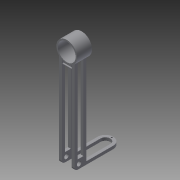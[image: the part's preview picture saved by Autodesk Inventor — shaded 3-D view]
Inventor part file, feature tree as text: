
AUTODESK INVENTOR PART (.ipt)
format: ipt  version: 2015 (Build 190159000, 159)  size: 225,792 bytes
history: native  units: mm
features: extrude x18, sketch x18, plane x2, fillet x1
ambient origin geometry x8: Origin, YZ Plane, XZ Plane, XY Plane, X Axis, Y Axis, Z Axis, Center Point
bodies: Solid1 (feature_tree)
feature tree (39):
  extrude  "Extrusion1"  Depth=2.25mm
  extrude  "Extrusion2"  Depth=2.0mm
  extrude  "Extrusion3"  Depth=10.5mm
  extrude  "Extrusion4"  Depth=2.0mm
  extrude  "Extrusion5"  Depth=2.0mm
  extrude  "Extrusion6"  Depth=2.0mm TaperAngle=0.0deg
  extrude  "Extrusion7"  Depth=6.0mm
  plane  "Work Plane1"
  extrude  "Extrusion8"  Depth=6.0mm
  plane  "Work Plane2"
  extrude  "Extrusion9"  Depth=6.0mm TaperAngle=0.0deg
  extrude  "Extrusion10"  Depth=2.0mm
  extrude  "Extrusion11"  Depth=6.0mm
  extrude  "Extrusion12"  Depth=4.0mm TaperAngle=0.0deg
  extrude  "Extrusion13"  TaperAngle=0.0deg  [1 undecoded]
  extrude  "Extrusion14"  Depth=2.0mm
  extrude  "Extrusion15"  Depth=1.5mm TaperAngle=0.0deg
  extrude  "Extrusion16"  Depth=1.5mm TaperAngle=0.0deg
  fillet  "Fillet4"  Radius=1.0mm
  extrude  "Extrusion17"  Depth=2.0mm
  extrude  "Extrusion18"  Depth=2.0mm
  sketch  "Sketch1"  dims[d0=15.0mm d1=2.25mm]
  sketch  "Sketch2"  dims[d2=2.0mm d3=4.5mm]
  sketch  "Sketch3"  dims[d4=2.0mm d5=10.5mm]
  sketch  "Sketch4"  dims[d6=10.75mm d7=2.0mm]
  sketch  "Sketch5"  dims[d8=13.0mm d9=2.0mm]
  sketch  "Sketch6"  dims[d10=2.0mm d11=60.0mm d12=0.0mm]
  sketch  "Sketch7"  dims[d13=2.0mm d14=6.0mm]
  sketch  "Sketch8"  dims[d15=4.0mm d16=0.0mm d17=6.0mm]
  sketch  "Sketch9"  dims[d18=3.0mm d19=6.0mm d20=0.0mm]
  sketch  "Sketch10"  dims[d22=2.0mm d23=2.0mm]
  sketch  "Sketch11"  dims[d24=20.0mm d25=0.0mm d27=6.0mm]
  sketch  "Sketch12"  dims[d28=4.0mm d29=0.0mm d30=4.0mm d31=0.0mm]
  sketch  "Sketch13"  dims[d33=20.0mm d34=0.0mm d35=0.0mm]
  sketch  "Sketch14"  dims[d36=2.0mm d37=0.0mm d38=60.0mm]
  sketch  "Sketch15"  dims[d42=10.0mm d43=0.0mm d44=1.5mm d45=0.0mm]
  sketch  "Sketch16"  dims[d46=1.0mm d47=0.0mm d48=1.5mm d49=0.0mm d50=1.0mm d51=0.0mm]
  sketch  "Sketch17"  dims[d52=2.0mm d53=2.0mm]
  sketch  "Sketch18"  dims[d54=2.0mm d55=2.0mm d56=59.5mm d57=0.0mm d58=1.0mm d59=0.0mm d60=1.0mm d61=0.0mm d62=2.0mm d63=1.0mm d64=2.0mm d65=0.0mm d66=1.0mm d67=8.0mm d68=0.0mm]
note: 1 required parameter value undecoded (feature->parameter linkage not recoverable at this tier; creation-order binding heuristic only, values carry confidence <= 0.55)
